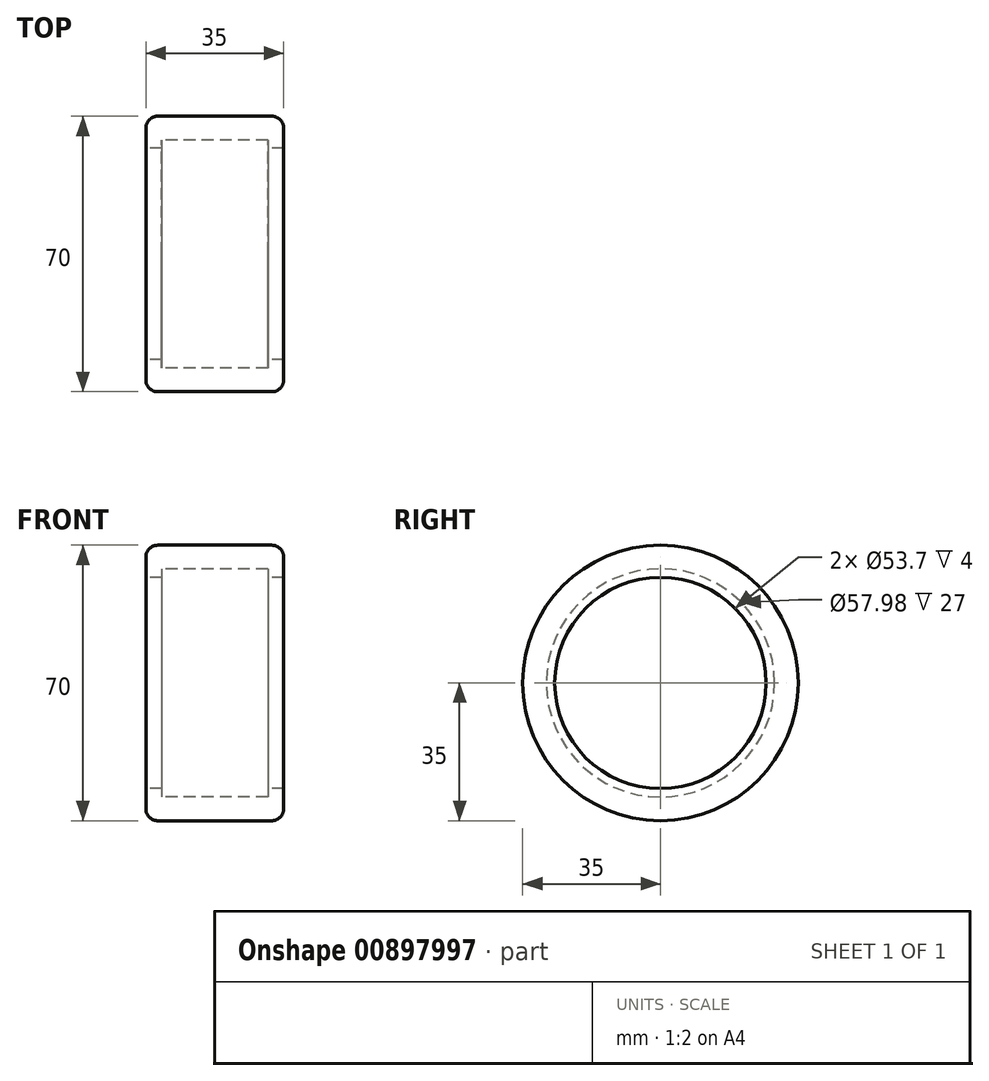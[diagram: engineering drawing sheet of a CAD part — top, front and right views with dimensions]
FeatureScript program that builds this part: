
annotation { "Feature Type Name" : "Feature", "Feature Type Description" : "" }
export const myFeature = defineFeature(function(context is Context, id is Id, definition is map)
    precondition{}
    {
        {
            var Q0;
            Q0=qCreatedBy(makeId("Front.planeOp"),FACE);
            var sketch = newSketch(context, id + "F0", { "sketchPlane" : qUnion([Q0])});
            skLineSegment(sketch, "E0", {"start": v(0, 0) * mm, "end": v(17.5, 0) * mm, "construction": true});
            skLineSegment(sketch, "E1", {"start": v(0, 0) * mm, "end": v(-17.5, 0) * mm, "construction": true});
            skLineSegment(sketch, "E2", {"start": v(-17.5, 0) * mm, "end": v(-17.5, 35) * mm, "construction": true});
            skLineSegment(sketch, "E3", {"start": v(-17.5, 35) * mm, "end": v(17.5, 35) * mm});
            skLineSegment(sketch, "E4", {"start": v(17.5, 35) * mm, "end": v(17.5, 26.85) * mm});
            skLineSegment(sketch, "E5", {"start": v(-17.5, 26.85) * mm, "end": v(-17.5, 35) * mm});
            skLineSegment(sketch, "E6", {"start": v(-17.5, 26.85) * mm, "end": v(-13.5, 26.85) * mm});
            skLineSegment(sketch, "E7", {"start": v(-13.5, 26.85) * mm, "end": v(-13.5, 28.99) * mm});
            skLineSegment(sketch, "E8", {"start": v(17.5, 26.85) * mm, "end": v(13.5, 26.85) * mm});
            skLineSegment(sketch, "E9", {"start": v(-13.5, 28.99) * mm, "end": v(13.5, 28.99) * mm});
            skLineSegment(sketch, "E10", {"start": v(13.5, 26.85) * mm, "end": v(13.5, 28.99) * mm});
            skSolve(sketch);
        }
        {
            var Q0;
            Q0=makeQuery(id+"F0.imprint","IMPRINT",FACE,{"disambiguationData":[TD([[makeQuery(id+"F0.imprint","IMPRINT",EDGE,{"derivedFrom":sQuery(id+"F0.wireOp",EDGE,"E3")}),-1.0]])]});
            var Q1;
            Q1=sQuery(id+"F0.wireOp",EDGE,"E0");
            revolve(context, id + "F1", {"surfaceOperationType" : NewSurfaceOperationType.NEW, "entities" : qUnion([Q0]), "axis" : qUnion([Q1]), "revolveType" : RevolveType.FULL});
        }
        {
            var Q0;
            Q0=makeQuery(id+"F1.opRevolve","SWEPT_EDGE",EDGE,{"disambiguationData":[OSD([sQuery(id+"F0.wireOp",EDGE,"E3"),sQuery(id+"F0.wireOp",EDGE,"E4")])]});
            var Q1;
            Q1=makeQuery(id+"F1.opRevolve","SWEPT_EDGE",EDGE,{"disambiguationData":[OSD([sQuery(id+"F0.wireOp",EDGE,"E3"),sQuery(id+"F0.wireOp",EDGE,"E5")])]});
            fillet(context, id + "F2", {"entities" : qUnion([Q0, Q1]), "radius" : 3 * mm, "tangentPropagation" : true, "allowEdgeOverflow" : false});
        }
    });
